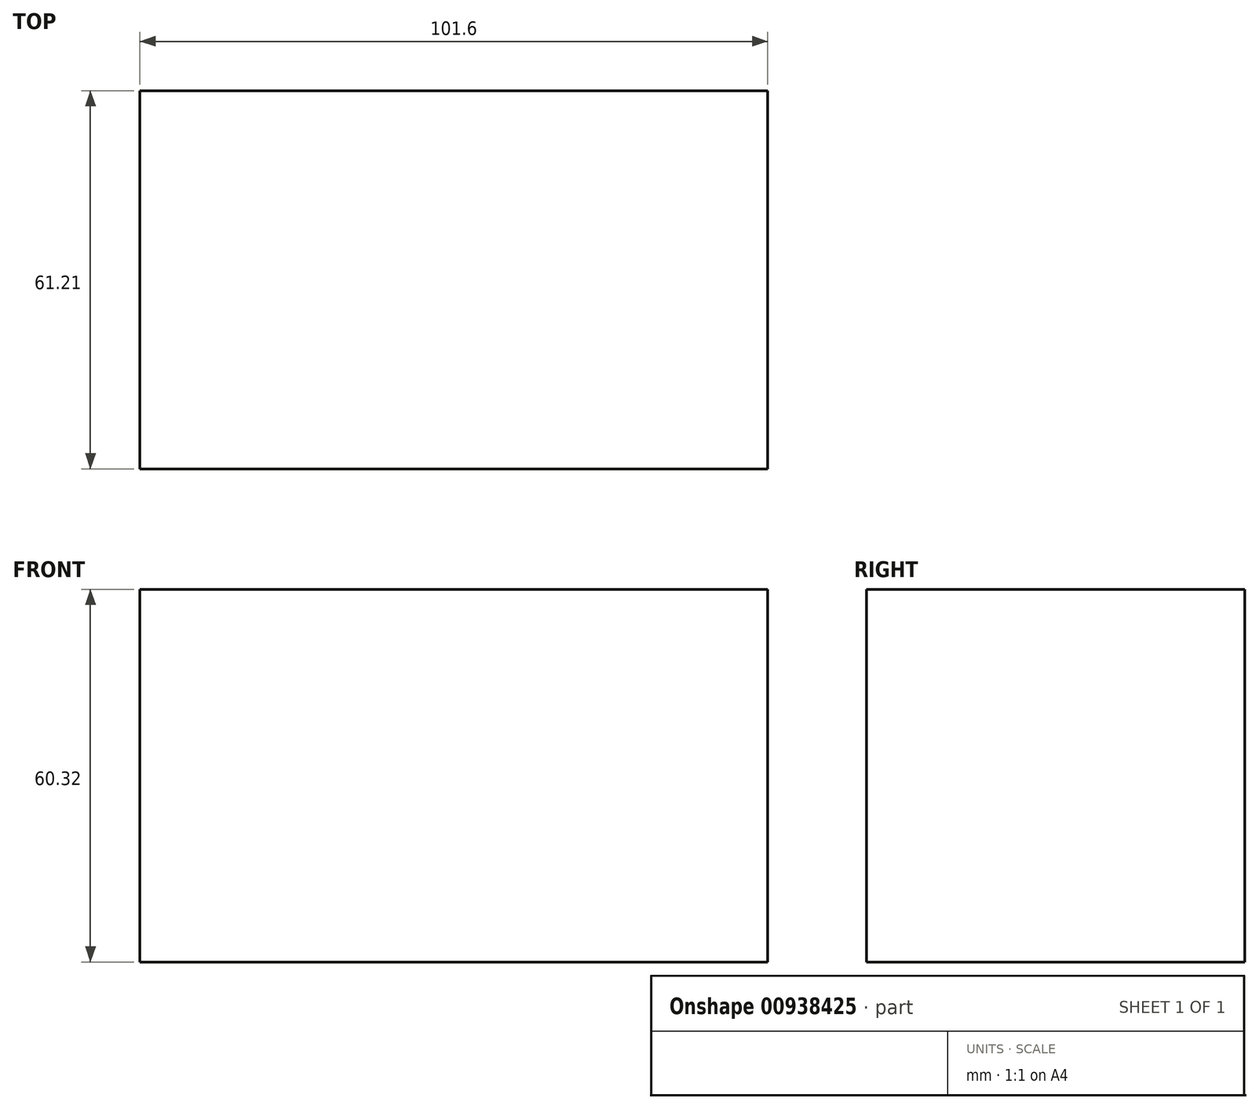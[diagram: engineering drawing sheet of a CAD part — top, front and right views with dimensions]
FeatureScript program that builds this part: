
annotation { "Feature Type Name" : "Feature", "Feature Type Description" : "" }
export const myFeature = defineFeature(function(context is Context, id is Id, definition is map)
    precondition{}
    {
        {
            var Q0;
            Q0=qCreatedBy(makeId("Front.planeOp"),FACE);
            var sketch = newSketch(context, id + "F0", { "sketchPlane" : qUnion([Q0])});
            skLineSegment(sketch, "E0", {"start": v(0, 0) * mm, "end": v(0, 60.33) * mm});
            skLineSegment(sketch, "E1", {"start": v(0, 60.33) * mm, "end": v(101.6, 60.33) * mm});
            skLineSegment(sketch, "E2", {"start": v(0, 0) * mm, "end": v(101.6, 0) * mm});
            skLineSegment(sketch, "E3", {"start": v(101.6, 0) * mm, "end": v(101.6, 60.33) * mm});
            skSolve(sketch);
        }
        {
            var Q0;
            Q0=makeQuery(id+"F0.imprint","IMPRINT",FACE,{"disambiguationData":[TD([[makeQuery(id+"F0.imprint","IMPRINT",EDGE,{"derivedFrom":sQuery(id+"F0.wireOp",EDGE,"E0")}),-1.0]])]});
            extrude(context, id + "F1", {"entities" : qUnion([Q0]), "depth" : 61.2 * mm, "offsetDistance" : 25.4 * mm});
        }
    });
